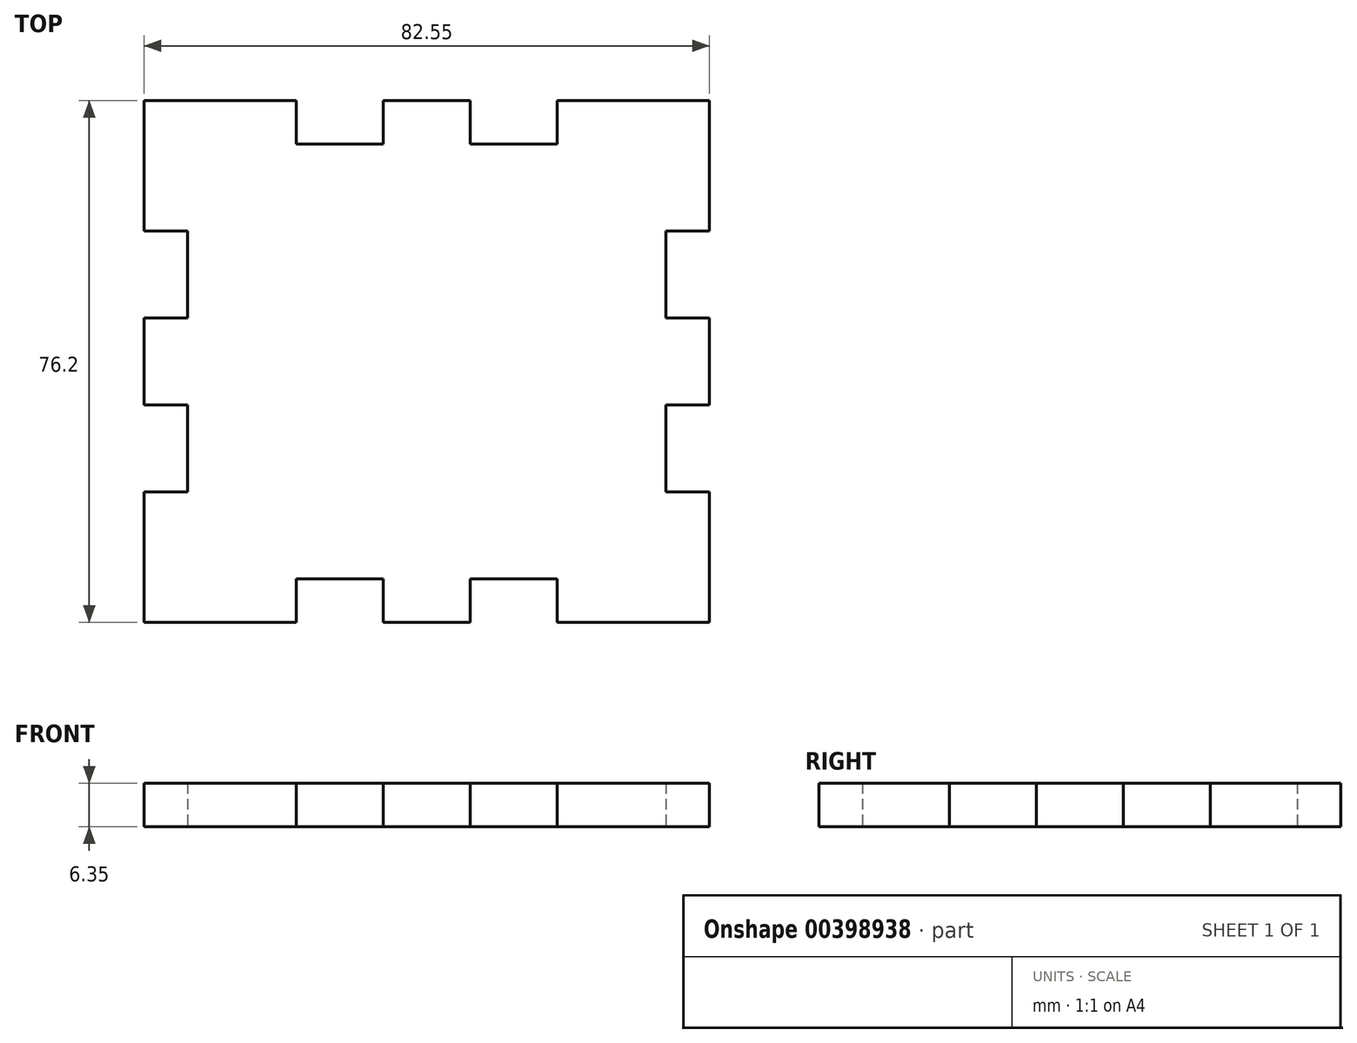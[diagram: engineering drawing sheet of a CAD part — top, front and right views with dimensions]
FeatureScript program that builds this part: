
annotation { "Feature Type Name" : "Feature", "Feature Type Description" : "" }
export const myFeature = defineFeature(function(context is Context, id is Id, definition is map)
    precondition{}
    {
        {
            var Q0;
            Q0=qCreatedBy(makeId("Top.planeOp"),FACE);
            var sketch = newSketch(context, id + "F0", { "sketchPlane" : qUnion([Q0])});
            skLineSegment(sketch, "E0.bottom", {"start": v(0, 0) * mm, "end": v(22.23, 0) * mm});
            skLineSegment(sketch, "E0.left", {"start": v(0, 0) * mm, "end": v(0, -19.05) * mm});
            skLineSegment(sketch, "E1", {"start": v(22.23, 0) * mm, "end": v(22.23, -6.35) * mm});
            skLineSegment(sketch, "E2", {"start": v(22.23, -6.35) * mm, "end": v(34.93, -6.35) * mm});
            skLineSegment(sketch, "E3", {"start": v(34.93, -6.35) * mm, "end": v(34.93, 0) * mm});
            skLineSegment(sketch, "E4", {"start": v(34.93, 0) * mm, "end": v(47.63, 0) * mm});
            skLineSegment(sketch, "E5", {"start": v(47.63, 0) * mm, "end": v(47.63, -6.35) * mm});
            skLineSegment(sketch, "E6", {"start": v(47.63, -6.35) * mm, "end": v(60.33, -6.35) * mm});
            skLineSegment(sketch, "E7", {"start": v(60.33, -6.35) * mm, "end": v(60.33, 0) * mm});
            skLineSegment(sketch, "E8.trimOffspring", {"start": v(60.33, 0) * mm, "end": v(82.55, 0) * mm});
            skLineSegment(sketch, "E9", {"start": v(0, -19.05) * mm, "end": v(6.35, -19.05) * mm});
            skLineSegment(sketch, "E10", {"start": v(6.35, -19.05) * mm, "end": v(6.35, -31.75) * mm});
            skLineSegment(sketch, "E11", {"start": v(6.35, -31.75) * mm, "end": v(0, -31.75) * mm});
            skLineSegment(sketch, "E12", {"start": v(0, -31.75) * mm, "end": v(0, -44.45) * mm});
            skLineSegment(sketch, "E13", {"start": v(0, -44.45) * mm, "end": v(6.35, -44.45) * mm});
            skLineSegment(sketch, "E14", {"start": v(6.35, -44.45) * mm, "end": v(6.35, -57.15) * mm});
            skLineSegment(sketch, "E15", {"start": v(6.35, -57.15) * mm, "end": v(0, -57.15) * mm});
            skLineSegment(sketch, "E16.trimOffspring", {"start": v(0, -57.15) * mm, "end": v(0, -76.2) * mm});
            skLineSegment(sketch, "E17", {"start": v(41.28, 0) * mm, "end": v(41.28, -27.3) * mm, "construction": true});
            skLineSegment(sketch, "E18", {"start": v(0, -38.1) * mm, "end": v(18.09, -38.1) * mm, "construction": true});
            skLineSegment(sketch, "E19.MirrorCS", {"start": v(82.55, 0) * mm, "end": v(82.55, -19.05) * mm});
            skLineSegment(sketch, "E20.MirrorCS", {"start": v(82.55, -19.05) * mm, "end": v(76.2, -19.05) * mm});
            skLineSegment(sketch, "E21.MirrorCS", {"start": v(76.2, -19.05) * mm, "end": v(76.2, -31.75) * mm});
            skLineSegment(sketch, "E22.MirrorCS", {"start": v(76.2, -31.75) * mm, "end": v(82.55, -31.75) * mm});
            skLineSegment(sketch, "E23.MirrorCS", {"start": v(82.55, -31.75) * mm, "end": v(82.55, -44.45) * mm});
            skLineSegment(sketch, "E24.MirrorCS", {"start": v(82.55, -44.45) * mm, "end": v(76.2, -44.45) * mm});
            skLineSegment(sketch, "E25.MirrorCS", {"start": v(76.2, -44.45) * mm, "end": v(76.2, -57.15) * mm});
            skLineSegment(sketch, "E26.MirrorCS", {"start": v(76.2, -57.15) * mm, "end": v(82.55, -57.15) * mm});
            skLineSegment(sketch, "E27.MirrorCS", {"start": v(82.55, -57.15) * mm, "end": v(82.55, -76.2) * mm});
            skLineSegment(sketch, "E28.MirrorCS", {"start": v(0, -76.2) * mm, "end": v(22.23, -76.2) * mm});
            skLineSegment(sketch, "E29.MirrorCS", {"start": v(22.23, -76.2) * mm, "end": v(22.23, -69.85) * mm});
            skLineSegment(sketch, "E30.MirrorCS", {"start": v(22.23, -69.85) * mm, "end": v(34.93, -69.85) * mm});
            skLineSegment(sketch, "E31.MirrorCS", {"start": v(34.93, -69.85) * mm, "end": v(34.93, -76.2) * mm});
            skLineSegment(sketch, "E32.MirrorCS", {"start": v(34.93, -76.2) * mm, "end": v(47.63, -76.2) * mm});
            skLineSegment(sketch, "E33.MirrorCS", {"start": v(47.63, -76.2) * mm, "end": v(47.63, -69.85) * mm});
            skLineSegment(sketch, "E34.MirrorCS", {"start": v(47.63, -69.85) * mm, "end": v(60.33, -69.85) * mm});
            skLineSegment(sketch, "E35.MirrorCS", {"start": v(60.33, -69.85) * mm, "end": v(60.33, -76.2) * mm});
            skLineSegment(sketch, "E36.MirrorCS", {"start": v(60.33, -76.2) * mm, "end": v(82.55, -76.2) * mm});
            skSolve(sketch);
        }
        {
            var Q0;
            Q0=makeQuery(id+"F0.imprint","IMPRINT",FACE,{"disambiguationData":[TD([[makeQuery(id+"F0.imprint","IMPRINT",EDGE,{"derivedFrom":sQuery(id+"F0.wireOp",EDGE,"E0.bottom")}),-1.0]])]});
            extrude(context, id + "F1", {"entities" : qUnion([Q0]), "depth" : 6.35 * mm, "offsetDistance" : 25.4 * mm});
        }
    });
